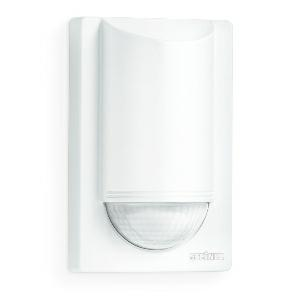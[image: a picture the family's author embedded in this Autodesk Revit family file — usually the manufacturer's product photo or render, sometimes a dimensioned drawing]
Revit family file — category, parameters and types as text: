
# Revit family: is_2180-2_603816
name_source: partatom
category: Elektroinstallationen
revit_build: Autodesk Revit 2016 (Build: 20190508_0715(x64)
units: mm (PartAtom-declared; Revit-internal decimal feet)

## family parameters
Basisbauteil = Fläche
Beim Laden mit Abzugskörper schneiden = Nein
Bemaßung runder Anschluss = Durchmesser verwenden
Beschriftungsausrichtung beibehalten = Nein
Gemeinsam genutzt = Nein
Raumberechnungspunkt = Nein
Teiletyp = Normal

## types (1)
- IS 2180-2
    Apparent Load = 0 VA
    Beschreibung = Type: Motion detectors; Dimensions (L x W x H): 55 x 78 x 120 mm; Mains power supply: 230 – 240 V / 50 Hz; Sensor Technology: passive infrared; Application, place: Indoors, Outdoors; Application, room: outdoors, front door, all round the building, terrace / balcony, courtyard & driveway; Installation site: wall, corner; Installation: Surface wiring; Switching zones: 504 switching zones; Electronic scalability: No; Mechanical scalability: No; Mounting height: 1,80 – 4,00 m; Optimum mounting height: 2 m; Detection angle: 180 °; Angle of aperture: 90 °; Sneak-by guard: Yes; Capability of masking out individual segments: Yes; Reach, radial: r = 2 m (6 m²) / r = 4 m (25 m²); Reach, tangential: r = 5 m (39 m²) / r = 12 m (226 m²); Twilight setting TEACH: No; Twilight setting: 2 – 2000 lx; Time setting: 5 sec – 15 min; Switching output 1, resistive: 1000 W; Switching output 1, number of LEDs / fluorescent lamps: 6 pcs.; Constant-lighting control: No; Basic light level function: No; Settings via: Potentiometers; With remote control: No; Interconnection: Yes; IP-rating: IP54; Material: Plastic; Ambient temperature: -20 – 50 °C; Colour: white; Colour, RAL: 9010; Manufacturer's Warranty: 5 years; Version: white; PU1, EAN: 4007841603816
    Height = 120 mm  [stored 0.393701 ft]
    Hersteller = Steinel
    Length = 55 mm
    Maximum range = 14.375 m
    ModVariant = Nein
    Modell = 603816
    Mounting Type = Surface mounted
    Number of Poles = 1
    OnlyDefault = Ja
    Power Factor = 1
    Product Name = IS 2180-2
    Product group = Sensor-switched indoor light
    ProductGroupID = 30
    Protection Class = Protection class
    Protection Degree = IP 54
    RlxData = <blob elided: 155317 chars, md5=f7d84a48>
    Sensor characteristics = Semi circular 145°-300°
    Sensor type = Passive (infrared)
    SensorDataFile = <blob elided: 4407 chars, md5=e7ee70d0>
    Type of entry = Motion
    Typenbild = produkt1_603816.jpg
    Typenkommentare = Product without accessories
    URL = http://relux.com
    VarID = ---
    Voltage = 0 V
    Vorgabe-Ansicht = 1800 mm
    Weight = 0.00 kg
    Width = 78 mm  [stored 0.255906 ft]

note: [stored X ft] marks values corroborated as IEEE doubles in the binary element streams (Revit-internal decimal feet)

## geometry (parser evidence)
native form markers: Blend x4, Sweep x21
no freeform markers — native parametric forms only
